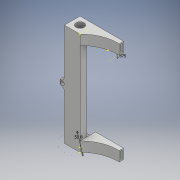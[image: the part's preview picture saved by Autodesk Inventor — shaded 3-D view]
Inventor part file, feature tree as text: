
AUTODESK INVENTOR PART (.ipt)
format: ipt  version: 2018 (Build 220112000, 112)  size: 239,616 bytes
history: native  units: mm
features: sketch x17, extrude x11, fillet x2
ambient origin geometry x8: Origin, YZ Plane, XZ Plane, XY Plane, X Axis, Y Axis, Z Axis, Center Point
bodies: Solid1 (feature_tree)
feature tree (30):
  extrude  "Extrusion1"  Depth=165.0mm
  extrude  "Extrusion2"  Depth=7.0mm
  sketch  "Sketch3"  dims[d5=7.0mm d6=22.0mm d7=0.0mm]
  extrude  "Extrusion3"  Depth=22.0mm TaperAngle=0.0deg
  extrude  "Extrusion4"  Depth=5.0mm TaperAngle=0.0deg
  extrude  "Extrusion5"  Depth=10.0mm
  sketch  "Sketch7"  dims[d18=7.5mm d19=0.0mm d20=2.0mm]
  sketch  "Sketch8"  dims[d21=16.0mm d22=16.0mm]
  extrude  "Extrusion6"  Depth=5.0mm
  fillet  "Fillet1"  Radius=5.0mm
  extrude  "Extrusion7"  Depth=2.0mm
  extrude  "Extrusion8"  Depth=16.0mm
  sketch  "Sketch12"  dims[d31=40.0mm d32=0.0mm]
  extrude  "Extrusion9"  Depth=45.0mm
  sketch  "Sketch14"  dims[d34=7.0mm]
  sketch  "Sketch15"  dims[d35=60.0mm]
  extrude  "Extrusion10"  Depth=3.25mm
  extrude  "Extrusion11"  Depth=12.25mm
  fillet  "Fillet2"  Radius=3.25mm
  sketch  "Sketch1"  dims[d0=25.0mm d1=165.0mm]
  sketch  "Sketch2"  dims[d2=3.0mm d3=0.0mm d4=7.0mm]
  sketch  "Sketch4"  dims[d8=13.0mm d9=5.0mm d10=0.0mm]
  sketch  "Sketch5"  dims[d11=5.0mm d12=0.0mm d13=10.0mm]
  sketch  "Sketch6"  dims[d14=165.0mm d15=0.0mm d16=5.0mm d17=5.0mm]
  sketch  "Sketch9"  dims[d23=45.0mm d24=0.0mm d25=3.5mm]
  sketch  "Sketch10"  dims[d26=12.25mm d27=3.25mm]
  sketch  "Sketch11"  dims[d28=3.5mm d29=12.25mm d30=3.25mm]
  sketch  "Sketch13"  dims[d33=1.875mm]
  sketch  "Sketch16"  dims[d36=165.0mm d37=0.0mm]
  sketch  "Sketch17"  dims[d38=50.8mm d39=7.0mm d40=3.5mm d41=3.5mm d42=10.5mm d43=0.0mm d44=6.35mm d45=10.5mm d46=0.0mm d47=7.0mm]
